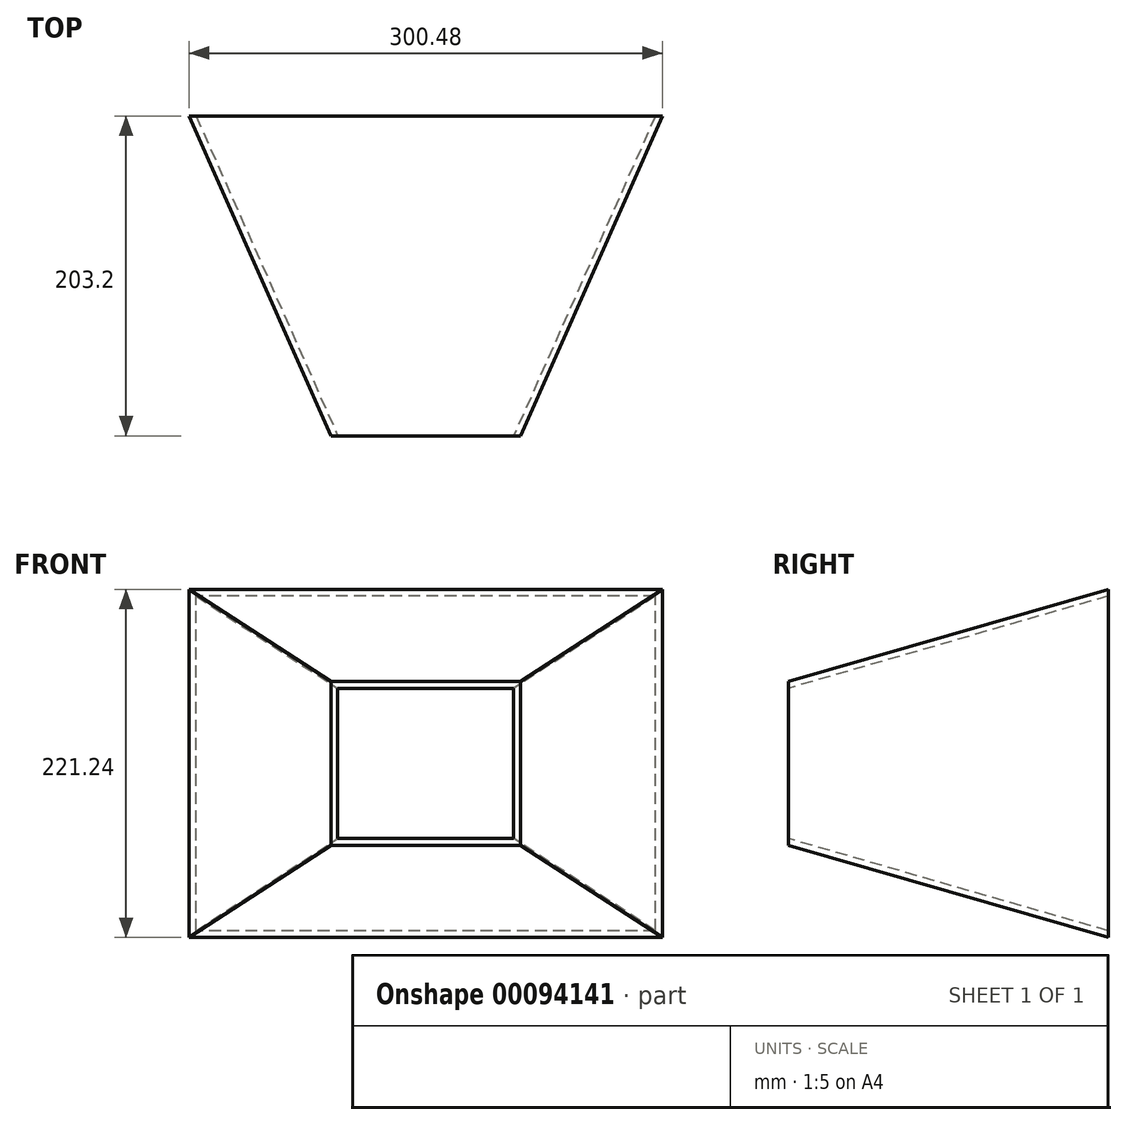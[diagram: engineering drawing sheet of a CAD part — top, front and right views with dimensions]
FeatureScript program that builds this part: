
annotation { "Feature Type Name" : "Feature", "Feature Type Description" : "" }
export const myFeature = defineFeature(function(context is Context, id is Id, definition is map)
    precondition{}
    {
        {
            var Q0;
            Q0=qCreatedBy(makeId("Front.planeOp"),FACE);
            var sketch = newSketch(context, id + "F0", { "sketchPlane" : qUnion([Q0])});
            skLineSegment(sketch, "E0.bottom", {"start": v(60.2, -52.07) * mm, "end": v(-60.2, -52.07) * mm});
            skLineSegment(sketch, "E0.top", {"start": v(60.2, 52.07) * mm, "end": v(-60.2, 52.07) * mm});
            skLineSegment(sketch, "E0.left", {"start": v(60.2, -52.07) * mm, "end": v(60.2, 52.07) * mm});
            skLineSegment(sketch, "E0.right", {"start": v(-60.2, -52.07) * mm, "end": v(-60.2, 52.07) * mm});
            skPoint(sketch, "E0.middle", {"position": v(0, 0) * mm});
            skPoint(sketch, "E1", {"position": v(0, 52.07) * mm});
            skPoint(sketch, "E2.bottom.end.orphan", {"position": v(51.56, -43.43) * mm});
            skPoint(sketch, "E2.left.start.orphan", {"position": v(-51.56, -43.43) * mm});
            skPoint(sketch, "E2.top.end.orphan", {"position": v(51.56, 43.43) * mm});
            skPoint(sketch, "E2.top.start.orphan", {"position": v(-51.56, 43.43) * mm});
            skSolve(sketch);
        }
        {
            var Q0;
            Q0=qCreatedBy(makeId("Front.planeOp"),FACE);
            cPlane(context, id + "F1", {"entities" : qUnion([Q0]), "cplaneType" : CPlaneType.OFFSET, "offset" : 203.2 * mm, "oppositeDirection" : true, "width" : 152.4 * mm, "height" : 152.4 * mm});
        }
        {
            var Q0;
            Q0=qCreatedBy(id+"F1.planeOp",FACE);
            var sketch = newSketch(context, id + "F2", { "sketchPlane" : qUnion([Q0])});
            skPoint(sketch, "E3.middle", {"position": v(0, 0) * mm});
            skLineSegment(sketch, "E4.bottom", {"start": v(150.24, -110.62) * mm, "end": v(-150.24, -110.62) * mm});
            skLineSegment(sketch, "E4.top", {"start": v(150.24, 110.62) * mm, "end": v(-150.24, 110.62) * mm});
            skLineSegment(sketch, "E4.left", {"start": v(150.24, -110.62) * mm, "end": v(150.24, 110.62) * mm});
            skLineSegment(sketch, "E4.right", {"start": v(-150.24, -110.62) * mm, "end": v(-150.24, 110.62) * mm});
            skPoint(sketch, "E5", {"position": v(0, 110.62) * mm});
            skPoint(sketch, "E3.top.start.orphan", {"position": v(141.6, -101.98) * mm});
            skPoint(sketch, "E3.bottom.start.orphan", {"position": v(141.6, 101.98) * mm});
            skPoint(sketch, "E3.right.end.orphan", {"position": v(-141.6, -101.98) * mm});
            skPoint(sketch, "E3.right.start.orphan", {"position": v(-141.6, 101.98) * mm});
            skSolve(sketch);
        }
        {
            var Q0;
            Q0=makeQuery(id+"F0.imprint","IMPRINT",FACE,{"disambiguationData":[TD([[makeQuery(id+"F0.imprint","IMPRINT",EDGE,{"derivedFrom":sQuery(id+"F0.wireOp",EDGE,"E0.bottom")}),-1.0]])]});
            var Q1;
            Q1=makeQuery(id+"F2.imprint","IMPRINT",FACE,{"disambiguationData":[TD([[makeQuery(id+"F2.imprint","IMPRINT",EDGE,{"derivedFrom":sQuery(id+"F2.wireOp",EDGE,"E4.bottom")}),-1.0]])]});
            loft(context, id + "F3", {"sheetProfilesArray" : [{ "sheetProfileEntities" : qUnion([Q0]) }, { "sheetProfileEntities" : qUnion([Q1]) }]});
        }
        {
            var Q0;
            Q0=makeQuery(id+"F3.opLoft","CAP_FACE",FACE,{"disambiguationData":[OSD([makeQuery(id+"F0.imprint","IMPRINT",FACE,{"disambiguationData":[TD([[makeQuery(id+"F0.imprint","IMPRINT",EDGE,{"derivedFrom":sQuery(id+"F0.wireOp",EDGE,"E0.bottom")}),-1.0]])]})])],"isStart":true});
            var sketch = newSketch(context, id + "F4", { "sketchPlane" : qUnion([Q0])});
            skLineSegment(sketch, "E6.bottom", {"start": v(-55.88, 47.75) * mm, "end": v(55.88, 47.75) * mm});
            skLineSegment(sketch, "E6.top", {"start": v(-55.88, -47.75) * mm, "end": v(55.88, -47.75) * mm});
            skLineSegment(sketch, "E6.left", {"start": v(-55.88, 47.75) * mm, "end": v(-55.88, -47.75) * mm});
            skLineSegment(sketch, "E6.right", {"start": v(55.88, 47.75) * mm, "end": v(55.88, -47.75) * mm});
            skPoint(sketch, "E6.middle", {"position": v(0, 0) * mm});
            skSolve(sketch);
        }
        {
            var Q0;
            Q0=makeQuery(id+"F3.opLoft","CAP_FACE",FACE,{"disambiguationData":[OSD([makeQuery(id+"F2.imprint","IMPRINT",FACE,{"disambiguationData":[TD([[makeQuery(id+"F2.imprint","IMPRINT",EDGE,{"derivedFrom":sQuery(id+"F2.wireOp",EDGE,"E4.bottom")}),-1.0]])]})])],"isStart":true});
            var sketch = newSketch(context, id + "F5", { "sketchPlane" : qUnion([Q0])});
            skLineSegment(sketch, "E7.bottom", {"start": v(-145.92, -106.3) * mm, "end": v(145.92, -106.3) * mm});
            skLineSegment(sketch, "E7.top", {"start": v(-145.92, 106.3) * mm, "end": v(145.92, 106.3) * mm});
            skLineSegment(sketch, "E7.left", {"start": v(-145.92, -106.3) * mm, "end": v(-145.92, 106.3) * mm});
            skLineSegment(sketch, "E7.right", {"start": v(145.92, -106.3) * mm, "end": v(145.92, 106.3) * mm});
            skPoint(sketch, "E7.middle", {"position": v(0, 0) * mm});
            skSolve(sketch);
        }
        {
            var Q1;
            Q1=makeQuery(id+"F5.imprint","IMPRINT",FACE,{"disambiguationData":[TD([[makeQuery(id+"F5.imprint","IMPRINT",EDGE,{"derivedFrom":sQuery(id+"F5.wireOp",EDGE,"E7.bottom")}),1.0]])]});
            var Q2;
            Q2=makeQuery(id+"F4.imprint","IMPRINT",FACE,{"disambiguationData":[TD([[makeQuery(id+"F4.imprint","IMPRINT",EDGE,{"derivedFrom":sQuery(id+"F4.wireOp",EDGE,"E6.bottom")}),-1.0]])]});
            loft(context, id + "F6", {"operationType" : NewBodyOperationType.REMOVE, "sheetProfilesArray" : [{ "sheetProfileEntities" : qUnion([Q1]) }, { "sheetProfileEntities" : qUnion([Q2]) }]});
        }
    });
